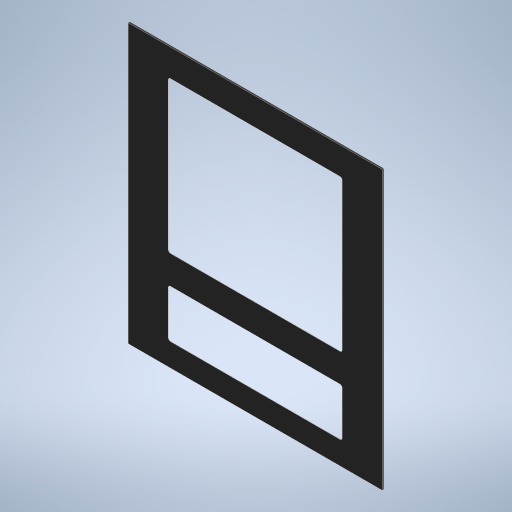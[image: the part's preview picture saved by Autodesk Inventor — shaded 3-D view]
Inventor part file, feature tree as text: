
AUTODESK INVENTOR PART (.ipt)
format: ipt  version: 2024 (Build 280153000, 153)  size: 304,640 bytes
history: native  units: mm
features: extrude x3, sketch x3, fillet x1, projected_geometry x1
ambient origin geometry x8: Origin, YZ Plane, XZ Plane, XY Plane, X Axis, Y Axis, Z Axis, Center Point
bodies: Solid1 (feature_tree)
feature tree (8):
  extrude  "Extrusion1"  Depth=510.0mm
  extrude  "Extrusion2"  Depth=73.5mm
  fillet  "Fillet1"  Radius=50.0mm
  extrude  "Extrusion3"  Depth=52.0mm
  sketch  "Sketch1"  dims[d0=466.0mm d1=510.0mm]
  sketch  "Sketch2"  dims[d2=3.0mm d3=0.0mm d4=73.5mm d6=50.0mm]
  sketch  "Sketch3"  dims[d7=278.0mm d8=52.0mm d9=88.0mm d10=0.0mm d11=0.0mm d12=4.0mm d13=15.0mm d14=15.0mm d15=2.38125mm d16=0.0mm]
  projected_geometry  "Projected Loop1"
